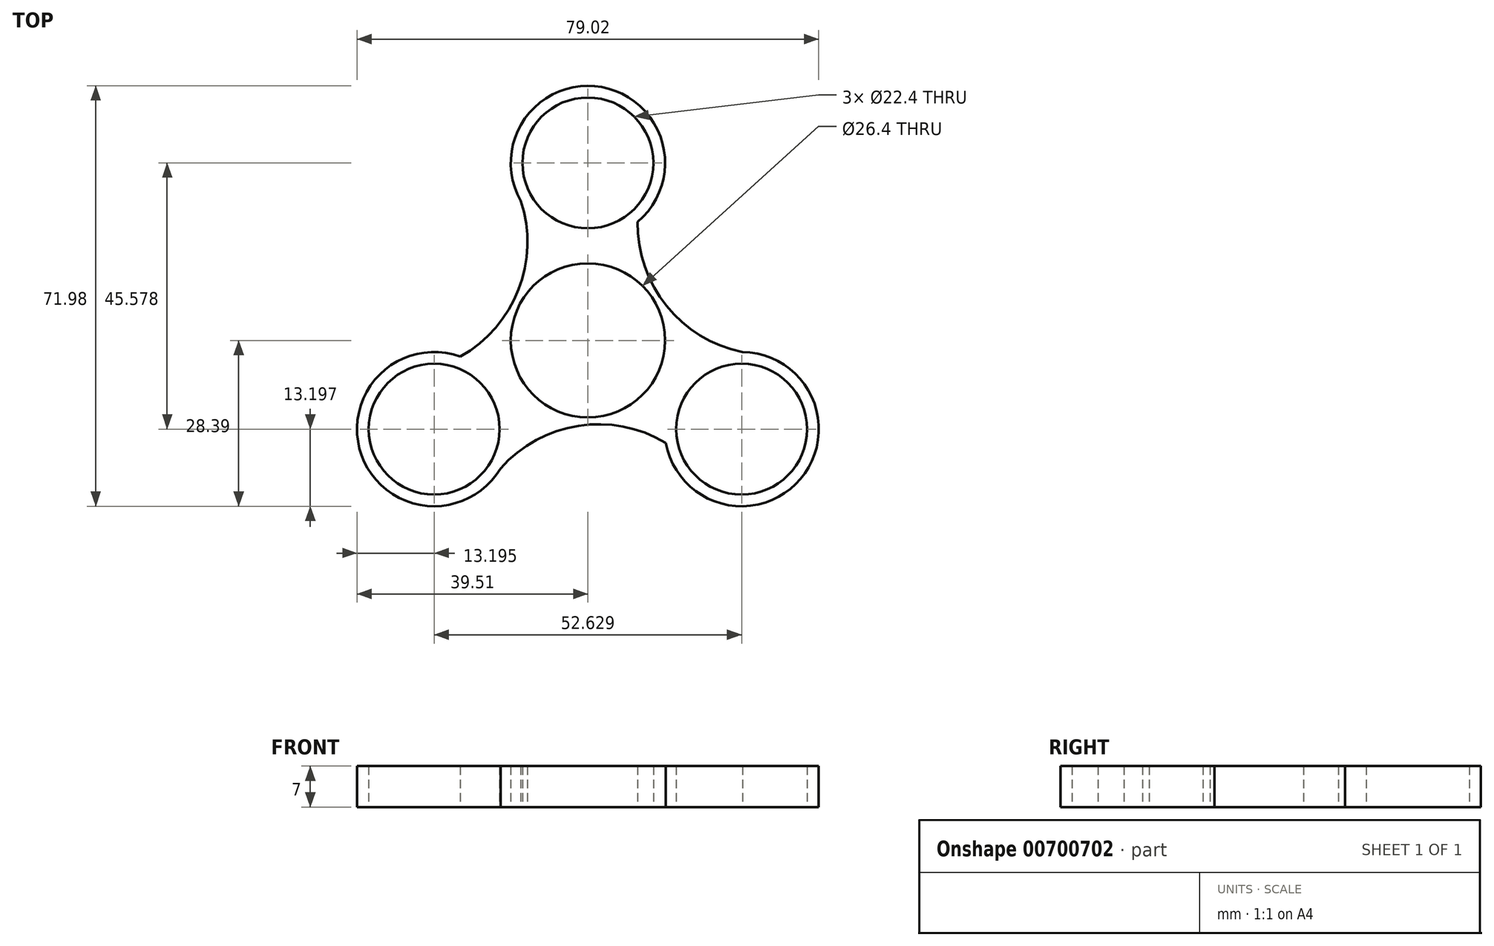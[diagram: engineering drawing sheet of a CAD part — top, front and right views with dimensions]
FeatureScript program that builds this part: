
annotation { "Feature Type Name" : "Feature", "Feature Type Description" : "" }
export const myFeature = defineFeature(function(context is Context, id is Id, definition is map)
    precondition{}
    {
        {
            var Q0;
            Q0=qCreatedBy(makeId("Top.planeOp"),FACE);
            var sketch = newSketch(context, id + "F0", { "sketchPlane" : qUnion([Q0])});
            skCircle(sketch, "E0", {"center": v(0, 0) * mm, "radius": 11.2 * mm});
            skCircle(sketch, "E1", {"center": v(0, 0) * mm, "radius": 13.2 * mm});
            skCircle(sketch, "E2", {"center": v(0, 30.39) * mm, "radius": 11.2 * mm});
            skArc(sketch, "E3", {"start": v(8.53, 20.31) * mm, "mid": v(2.34, 43.38) * mm, "end": v(-11.51, 23.93) * mm});
            skArc(sketch, "E4.1.0", {"start": v(-21.85, -2.77) * mm, "mid": v(-38.74, -19.66) * mm, "end": v(-14.96, -21.93) * mm});
            skCircle(sketch, "E4.1.1", {"center": v(-26.31, -15.2) * mm, "radius": 11.2 * mm});
            skArc(sketch, "E4.2.0", {"start": v(13.33, -17.54) * mm, "mid": v(36.4, -23.72) * mm, "end": v(26.48, -2) * mm});
            skCircle(sketch, "E4.2.1", {"center": v(26.31, -15.2) * mm, "radius": 11.2 * mm});
            skArc(sketch, "E5", {"start": v(-21.85, -2.77) * mm, "mid": v(-11.86, 8.7) * mm, "end": v(-11.51, 23.93) * mm});
            skArc(sketch, "E6.1.0", {"start": v(13.33, -17.54) * mm, "mid": v(-1.61, -14.62) * mm, "end": v(-14.96, -21.93) * mm});
            skArc(sketch, "E6.2.0", {"start": v(8.53, 20.31) * mm, "mid": v(13.47, 5.91) * mm, "end": v(26.48, -2) * mm});
            skSolve(sketch);
        }
        {
            var Q0;
            Q0=makeQuery(id+"F0.imprint","IMPRINT",FACE,{"disambiguationData":[TD([[makeQuery(id+"F0.imprint","IMPRINT",EDGE,{"derivedFrom":sQuery(id+"F0.wireOp",EDGE,"E1")}),-1.0]])]});
            extrude(context, id + "F1", {"entities" : qUnion([Q0]), "depth" : 7 * mm, "offsetDistance" : 25 * mm});
        }
    });
